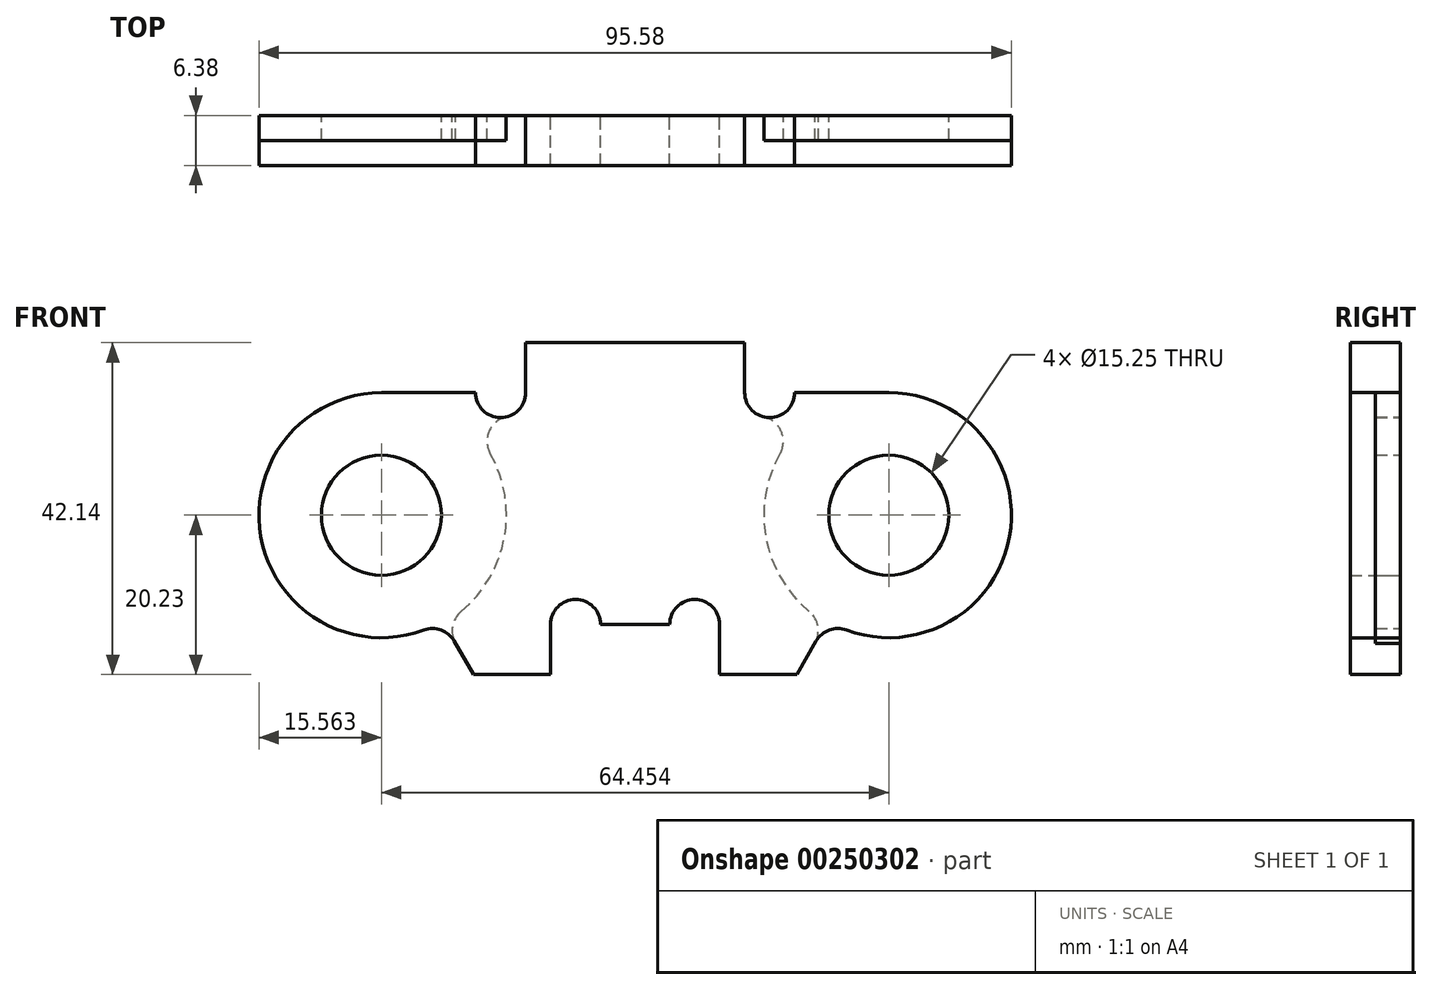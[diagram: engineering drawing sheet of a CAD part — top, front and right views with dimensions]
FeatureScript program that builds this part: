
annotation { "Feature Type Name" : "Feature", "Feature Type Description" : "" }
export const myFeature = defineFeature(function(context is Context, id is Id, definition is map)
    precondition{}
    {
        {
            var Q0;
            Q0=qCreatedBy(makeId("Front.planeOp"),FACE);
            var sketch = newSketch(context, id + "F0", { "sketchPlane" : qUnion([Q0])});
            skArc(sketch, "E0", {"start": v(26.84, -14.6) * mm, "mid": v(24.66, -14.6) * mm, "end": v(23, -16) * mm});
            skLineSegment(sketch, "E1", {"start": v(20.55, -20.23) * mm, "end": v(23, -16) * mm});
            skLineSegment(sketch, "E2", {"start": v(10.74, -20.23) * mm, "end": v(20.55, -20.23) * mm});
            skLineSegment(sketch, "E3", {"start": v(10.74, -13.88) * mm, "end": v(10.74, -20.23) * mm});
            skArc(sketch, "E4", {"start": v(10.74, -13.88) * mm, "mid": v(7.57, -10.7) * mm, "end": v(4.4, -13.88) * mm});
            skLineSegment(sketch, "E5", {"start": v(-4.4, -13.88) * mm, "end": v(4.4, -13.88) * mm});
            skArc(sketch, "E6", {"start": v(-4.4, -13.88) * mm, "mid": v(-7.57, -10.7) * mm, "end": v(-10.74, -13.88) * mm});
            skLineSegment(sketch, "E7", {"start": v(-10.74, -20.23) * mm, "end": v(-10.74, -13.88) * mm});
            skLineSegment(sketch, "E8", {"start": v(-20.55, -20.23) * mm, "end": v(-10.74, -20.23) * mm});
            skLineSegment(sketch, "E9", {"start": v(-23, -16) * mm, "end": v(-20.55, -20.23) * mm});
            skArc(sketch, "E10", {"start": v(-23, -16) * mm, "mid": v(-24.66, -14.6) * mm, "end": v(-26.84, -14.6) * mm});
            skArc(sketch, "E11", {"start": v(-32.23, 15.56) * mm, "mid": v(-47.55, -2.74) * mm, "end": v(-26.84, -14.6) * mm});
            skLineSegment(sketch, "E12", {"start": v(-20.27, 15.56) * mm, "end": v(-32.23, 15.56) * mm});
            skArc(sketch, "E13", {"start": v(-20.27, 15.56) * mm, "mid": v(-17.1, 12.39) * mm, "end": v(-13.92, 15.56) * mm});
            skLineSegment(sketch, "E14", {"start": v(-13.92, 21.91) * mm, "end": v(-13.92, 15.56) * mm});
            skLineSegment(sketch, "E15", {"start": v(13.92, 21.91) * mm, "end": v(-13.92, 21.91) * mm});
            skLineSegment(sketch, "E16", {"start": v(13.92, 15.56) * mm, "end": v(13.92, 21.91) * mm});
            skArc(sketch, "E17", {"start": v(13.92, 15.56) * mm, "mid": v(17.1, 12.39) * mm, "end": v(20.27, 15.56) * mm});
            skLineSegment(sketch, "E18", {"start": v(32.23, 15.56) * mm, "end": v(20.27, 15.56) * mm});
            skArc(sketch, "E19", {"start": v(26.84, -14.6) * mm, "mid": v(47.55, -2.74) * mm, "end": v(32.23, 15.56) * mm});
            skArc(sketch, "E20", {"start": v(-22.1, -12.23) * mm, "mid": v(-16.62, -2.88) * mm, "end": v(-18.41, 7.82) * mm});
            skArc(sketch, "E21", {"start": v(22.84, -16.27) * mm, "mid": v(23.21, -14.12) * mm, "end": v(22.1, -12.23) * mm});
            skArc(sketch, "E22", {"start": v(18.41, 7.82) * mm, "mid": v(16.62, -2.88) * mm, "end": v(22.1, -12.23) * mm});
            skArc(sketch, "E23", {"start": v(18.41, 7.82) * mm, "mid": v(18.55, 10.66) * mm, "end": v(16.37, 12.47) * mm});
            skCircle(sketch, "E24", {"center": v(32.23, 0) * mm, "radius": 7.63 * mm});
            skCircle(sketch, "E25", {"center": v(-32.23, 0) * mm, "radius": 7.63 * mm});
            skArc(sketch, "E26", {"start": v(-16.37, 12.47) * mm, "mid": v(-18.55, 10.66) * mm, "end": v(-18.41, 7.82) * mm});
            skArc(sketch, "E27", {"start": v(-22.1, -12.23) * mm, "mid": v(-23.21, -14.12) * mm, "end": v(-22.84, -16.27) * mm});
            skSolve(sketch);
        }
        {
            var Q0;
            Q0=makeQuery(id+"F0.imprint","IMPRINT",FACE,{"disambiguationData":[TD([[makeQuery(id+"F0.imprint","IMPRINT",EDGE,{"derivedFrom":sQuery(id+"F0.wireOp",EDGE,"E25")}),-1.0]])]});
            var Q1;
            {var subQ7=sQuery(id+"F0.wireOp",EDGE,"E2");Q1=makeQuery(id+"F0.imprint","IMPRINT",FACE,{"disambiguationData":[TD([[makeQuery(id+"F0.imprint","IMPRINT",EDGE,{"derivedFrom":subQ7}),1.0]])]});}
            var Q2;
            Q2=makeQuery(id+"F0.imprint","IMPRINT",FACE,{"disambiguationData":[TD([[makeQuery(id+"F0.imprint","IMPRINT",EDGE,{"derivedFrom":sQuery(id+"F0.wireOp",EDGE,"E24")}),-1.0]])]});
            extrude(context, id + "F1", {"entities" : qUnion([Q0, Q1, Q2]), "depth" : 6.38 * mm});
        }
        {
            var Q0;
            {var subQ2=sQuery(id+"F0.wireOp",EDGE,"E10");Q0=makeQuery(id+"F0.imprint","IMPRINT",FACE,{"disambiguationData":[TD([[makeQuery(id+"F0.imprint","IMPRINT",EDGE,{"derivedFrom":subQ2}),-1.0]])]});}
            var Q1;
            {var subQ2=sQuery(id+"F0.wireOp",EDGE,"E0");Q1=makeQuery(id+"F0.imprint","IMPRINT",FACE,{"disambiguationData":[TD([[makeQuery(id+"F0.imprint","IMPRINT",EDGE,{"derivedFrom":subQ2}),-1.0]])]});}
            extrude(context, id + "F2", {"entities" : qUnion([Q0, Q1]), "depth" : 3.17 * mm});
        }
    });
